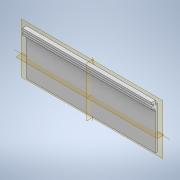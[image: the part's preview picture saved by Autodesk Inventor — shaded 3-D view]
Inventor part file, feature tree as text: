
AUTODESK INVENTOR PART (.ipt)
format: ipt  version: 2022.4 (Build 264492010, 492A)  size: 116,224 bytes
history: native  units: mm
features: extrude x1, sketch x1
ambient origin geometry x8: Origin, YZ Plane, XZ Plane, XY Plane, X Axis, Y Axis, Z Axis, Center Point
bodies: Solid1 (feature_tree)
feature tree (2):
  extrude  "Extrusion1"  Depth=1.6mm
  sketch  "Sketch2"  dims[d0=32.5mm d1=1.6mm d2=3.0mm d3=3.2mm d4=1.6mm d6=1.6mm d7=1.6mm d8=1.4mm d9=3.2mm d10=100.0mm d11=0.0mm d12=1.6mm]
